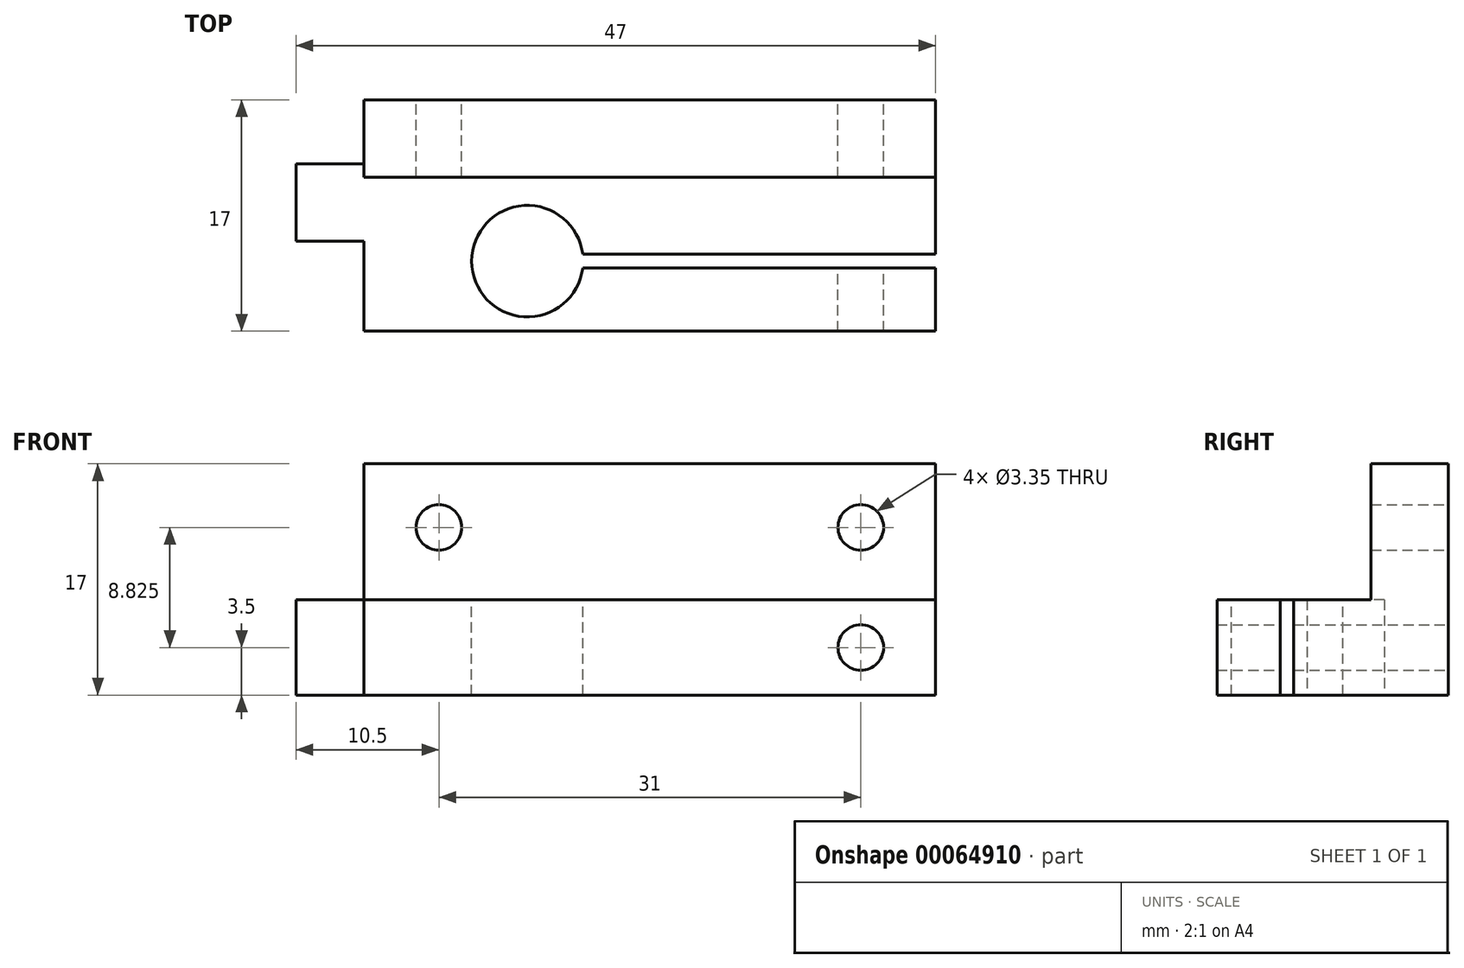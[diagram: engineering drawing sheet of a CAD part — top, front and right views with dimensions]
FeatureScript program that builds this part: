
annotation { "Feature Type Name" : "Feature", "Feature Type Description" : "" }
export const myFeature = defineFeature(function(context is Context, id is Id, definition is map)
    precondition{}
    {
        {
            var Q0;
            Q0=qCreatedBy(makeId("Top.planeOp"),FACE);
            var sketch = newSketch(context, id + "F0", { "sketchPlane" : qUnion([Q0])});
            skLineSegment(sketch, "E0.bottom", {"start": v(0, 0) * mm, "end": v(42, 0) * mm});
            skLineSegment(sketch, "E0.top", {"start": v(0, 17) * mm, "end": v(42, 17) * mm});
            skLineSegment(sketch, "E0.left", {"start": v(0, 0) * mm, "end": v(0, 17) * mm});
            skLineSegment(sketch, "E0.right", {"start": v(42, 0) * mm, "end": v(42, 17) * mm});
            skSolve(sketch);
        }
        {
            var Q0;
            Q0=qSketchRegion(id+"F0",true);
            extrude(context, id + "F1", {"entities" : qUnion([Q0]), "depth" : 7 * mm});
        }
        {
            var Q0;
            Q0=makeQuery(id+"F1.opExtrude","CAP_FACE",FACE,{"disambiguationData":[OSD([sQuery(id+"F0.wireOp",EDGE,"E0.bottom"),sQuery(id+"F0.wireOp",EDGE,"E0.top"),sQuery(id+"F0.wireOp",EDGE,"E0.left"),sQuery(id+"F0.wireOp",EDGE,"E0.right")])],"isStart":false});
            var sketch = newSketch(context, id + "F2", { "sketchPlane" : qUnion([Q0])});
            skCircle(sketch, "E1", {"center": v(12, 5.14) * mm, "radius": 4.1 * mm});
            skLineSegment(sketch, "E2", {"start": v(12, 5.14) * mm, "end": v(42, 5.14) * mm});
            skLineSegment(sketch, "E3", {"start": v(42, 5.14) * mm, "end": v(42, 4.64) * mm});
            skLineSegment(sketch, "E4", {"start": v(42, 4.64) * mm, "end": v(16.07, 4.64) * mm});
            skLineSegment(sketch, "E5", {"start": v(42, 5.14) * mm, "end": v(42, 5.64) * mm});
            skLineSegment(sketch, "E6", {"start": v(42, 5.64) * mm, "end": v(16.07, 5.64) * mm});
            skSolve(sketch);
        }
        {
            var Q0;
            Q0=makeQuery(id+"F1.opExtrude","SWEPT_FACE",FACE,{"disambiguationData":[OSD([sQuery(id+"F0.wireOp",EDGE,"E0.top")])]});
            var sketch = newSketch(context, id + "F3", { "sketchPlane" : qUnion([Q0])});
            skCircle(sketch, "E7", {"center": v(-36.5, 3.5) * mm, "radius": 1.68 * mm});
            skLineSegment(sketch, "E8", {"start": v(-36.5, 3.5) * mm, "end": v(-42, 3.5) * mm});
            skSolve(sketch);
        }
        {
            var Q0;
            Q0=qSketchRegion(id+"F3",true);
            extrude(context, id + "F4", {"entities" : qUnion([Q0]), "operationType" : NewBodyOperationType.REMOVE, "oppositeDirection" : true, "depth" : 25 * mm});
        }
        {
            var Q0;
            Q0=makeQuery(id+"F1.opExtrude","CAP_FACE",FACE,{"disambiguationData":[OSD([sQuery(id+"F0.wireOp",EDGE,"E0.bottom"),sQuery(id+"F0.wireOp",EDGE,"E0.top"),sQuery(id+"F0.wireOp",EDGE,"E0.left"),sQuery(id+"F0.wireOp",EDGE,"E0.right")])],"isStart":false});
            var sketch = newSketch(context, id + "F5", { "sketchPlane" : qUnion([Q0])});
            skLineSegment(sketch, "E9.bottom", {"start": v(0, 17) * mm, "end": v(42, 17) * mm});
            skLineSegment(sketch, "E9.top", {"start": v(0, 11.33) * mm, "end": v(42, 11.33) * mm});
            skLineSegment(sketch, "E9.left", {"start": v(0, 17) * mm, "end": v(0, 11.33) * mm});
            skLineSegment(sketch, "E9.right", {"start": v(42, 17) * mm, "end": v(42, 11.33) * mm});
            skSolve(sketch);
        }
        {
            var Q0;
            Q0=makeQuery(id+"F5.imprint","IMPRINT",FACE,{"disambiguationData":[TD([[makeQuery(id+"F5.imprint","IMPRINT",EDGE,{"derivedFrom":sQuery(id+"F5.wireOp",EDGE,"E9.bottom")}),-1.0]])]});
            extrude(context, id + "F6", {"entities" : qUnion([Q0]), "operationType" : NewBodyOperationType.ADD, "depth" : 10 * mm});
        }
        {
            var Q0;
            Q0=makeQuery(id+"F6.boolean.opBoolean","MERGE",FACE,{"derivedFrom":[makeQuery(id+"F1.opExtrude","SWEPT_FACE",FACE,{"disambiguationData":[OSD([sQuery(id+"F0.wireOp",EDGE,"E0.top")])]}),makeQuery(id+"F6.opExtrude","SWEPT_FACE",FACE,{"disambiguationData":[OSD([sQuery(id+"FFFDCbTcivKPk1C_1.wireOp",EDGE,"d29ae964-e38a-46b3-8ff4-cadffaec6662.bottom")])]})]});
            var sketch = newSketch(context, id + "F7", { "sketchPlane" : qUnion([Q0])});
            skPoint(sketch, "E10", {"position": v(-36.5, 3.5) * mm});
            skCircle(sketch, "E11", {"center": v(-36.5, 12.33) * mm, "radius": 1.68 * mm});
            skCircle(sketch, "E12", {"center": v(-5.5, 12.33) * mm, "radius": 1.68 * mm});
            skSolve(sketch);
        }
        {
            var Q0;
            Q0=qSketchRegion(id+"F7",true);
            extrude(context, id + "F8", {"entities" : qUnion([Q0]), "operationType" : NewBodyOperationType.REMOVE, "oppositeDirection" : true, "depth" : 25 * mm});
        }
        {
            var Q0;
            Q0=qSketchRegion(id+"F2",true);
            extrude(context, id + "F9", {"entities" : qUnion([Q0]), "operationType" : NewBodyOperationType.REMOVE, "oppositeDirection" : true, "depth" : 25 * mm});
        }
        {
            var Q0;
            Q0=makeQuery(id+"F6.boolean.opBoolean","MERGE",FACE,{"derivedFrom":[makeQuery(id+"F1.opExtrude","SWEPT_FACE",FACE,{"disambiguationData":[OSD([sQuery(id+"F0.wireOp",EDGE,"E0.left")])]}),makeQuery(id+"F6.opExtrude","SWEPT_FACE",FACE,{"disambiguationData":[OSD([sQuery(id+"F5.wireOp",EDGE,"E9.left")])]})]});
            var sketch = newSketch(context, id + "F11", { "sketchPlane" : qUnion([Q0])});
            skLineSegment(sketch, "E13.bottom", {"start": v(-12.3, 7) * mm, "end": v(-6.6, 7) * mm});
            skLineSegment(sketch, "E13.top", {"start": v(-12.3, 0) * mm, "end": v(-6.6, 0) * mm});
            skLineSegment(sketch, "E13.left", {"start": v(-12.3, 7) * mm, "end": v(-12.3, 0) * mm});
            skLineSegment(sketch, "E13.right", {"start": v(-6.6, 7) * mm, "end": v(-6.6, 0) * mm});
            skSolve(sketch);
        }
        {
            var Q0;
            Q0=qSketchRegion(id+"F11",true);
            extrude(context, id + "F12", {"entities" : qUnion([Q0]), "operationType" : NewBodyOperationType.ADD, "depth" : 5 * mm});
        }
    });
